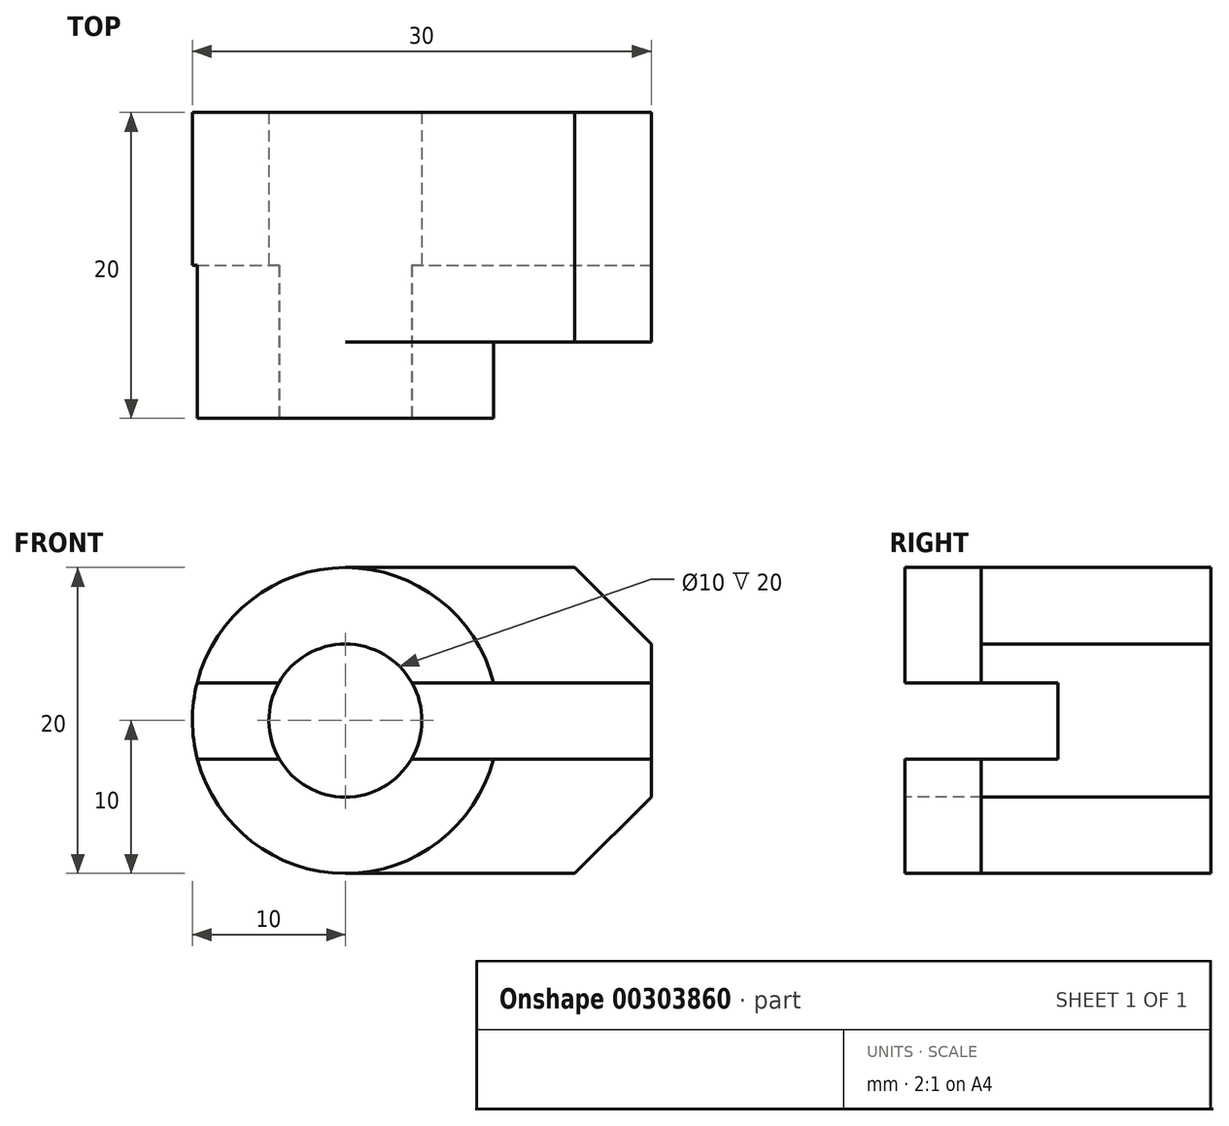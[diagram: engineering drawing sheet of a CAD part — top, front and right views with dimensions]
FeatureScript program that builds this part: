
annotation { "Feature Type Name" : "Feature", "Feature Type Description" : "" }
export const myFeature = defineFeature(function(context is Context, id is Id, definition is map)
    precondition{}
    {
        {
            var Q0;
            Q0=qCreatedBy(makeId("Front.planeOp"),FACE);
            var sketch = newSketch(context, id + "F0", { "sketchPlane" : qUnion([Q0])});
            skCircle(sketch, "E0", {"center": v(0, 0) * mm, "radius": 5 * mm});
            skCircle(sketch, "E1", {"center": v(0, 0) * mm, "radius": 10 * mm});
            skLineSegment(sketch, "E2", {"start": v(0, 10) * mm, "end": v(15, 10) * mm});
            skLineSegment(sketch, "E3", {"start": v(15, -10) * mm, "end": v(0, -10) * mm});
            skLineSegment(sketch, "E4", {"start": v(20, 5) * mm, "end": v(20, -5) * mm});
            skLineSegment(sketch, "E5", {"start": v(15, 10) * mm, "end": v(20, 5) * mm});
            skLineSegment(sketch, "E6", {"start": v(15, -10) * mm, "end": v(20, -5) * mm});
            skSolve(sketch);
        }
        {
            var Q0;
            Q0=makeQuery(id+"F0.imprint","IMPRINT",FACE,{"disambiguationData":[TD([[makeQuery(id+"F0.imprint","IMPRINT",EDGE,{"derivedFrom":sQuery(id+"F0.wireOp",EDGE,"E0")}),-1.0]])]});
            extrude(context, id + "F1", {"entities" : qUnion([Q0]), "oppositeDirection" : true, "depth" : 15 * mm, "hasSecondDirection" : true, "secondDirectionOppositeDirection" : false, "secondDirectionDepth" : 5 * mm});
        }
        {
            var Q0;
            {var subQ1=sQuery(id+"F0.wireOp",EDGE,"E2");Q0=makeQuery(id+"F0.imprint","IMPRINT",FACE,{"disambiguationData":[TD([[makeQuery(id+"F0.imprint","IMPRINT",EDGE,{"derivedFrom":subQ1}),-1.0]])]});}
            extrude(context, id + "F2", {"entities" : qUnion([Q0]), "operationType" : NewBodyOperationType.ADD, "oppositeDirection" : true, "depth" : 15 * mm});
        }
        {
            var Q0;
            Q0=qCreatedBy(makeId("Right.planeOp"),FACE);
            var sketch = newSketch(context, id + "F3", { "sketchPlane" : qUnion([Q0])});
            skLineSegment(sketch, "E7", {"start": v(0, 0) * mm, "end": v(0, 5) * mm});
            skLineSegment(sketch, "E8", {"start": v(-5, 2.47) * mm, "end": v(-5, -2.53) * mm});
            skLineSegment(sketch, "E9", {"start": v(-5, -2.53) * mm, "end": v(5, -2.53) * mm});
            skLineSegment(sketch, "E10", {"start": v(5, -2.53) * mm, "end": v(5, 2.47) * mm});
            skLineSegment(sketch, "E11", {"start": v(-5, 2.47) * mm, "end": v(5, 2.47) * mm});
            skSolve(sketch);
        }
        {
            var Q0;
            Q0 = qSketchRegion(id + "F3", true);
            extrude(context, id + "F4", {"entities" : qUnion([Q0]), "operationType" : NewBodyOperationType.REMOVE, "oppositeDirection" : true, "depth" : 25 * mm, "hasSecondDirection" : true, "secondDirectionOppositeDirection" : false, "secondDirectionDepth" : 25 * mm});
        }
    });
